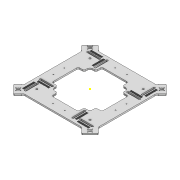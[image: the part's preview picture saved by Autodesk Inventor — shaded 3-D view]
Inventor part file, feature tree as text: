
AUTODESK INVENTOR PART (.ipt)
format: ipt  version: 2020 (Build 240168000, 168)  size: 1,201,152 bytes
history: native  units: mm
features: sketch x3, extrude x2, fillet x2, chamfer x1, mirror x1
ambient origin geometry x8: Origin, YZ Plane, XZ Plane, XY Plane, X Axis, Y Axis, Z Axis, Center Point
bodies: Solid1 (feature_tree)
feature tree (9):
  extrude  "Extrusion1"  Depth=3.0mm
  extrude  "Extrusion2"  Depth=10.0mm TaperAngle=0.0deg
  sketch  "Sketch4"  dims[d7=3.0mm d8=18.5mm d9=20.0mm d10=10.0mm d11=0.0mm d12=6.0mm d13=2.0mm d14=45.0deg d15=3.0mm d16=7.0mm]
  chamfer  "Chamfer1"  Distance=18.5mm
  fillet  "Fillet1"  Radius=20.0mm
  fillet  "Fillet2"  Radius=10.0mm
  sketch  "Sketch2"  dims[d2=20.0mm d3=3.0mm]
  sketch  "Sketch3"  dims[d4=20.0mm d5=10.0mm d6=0.0mm]
  mirror  "Mirror7"
